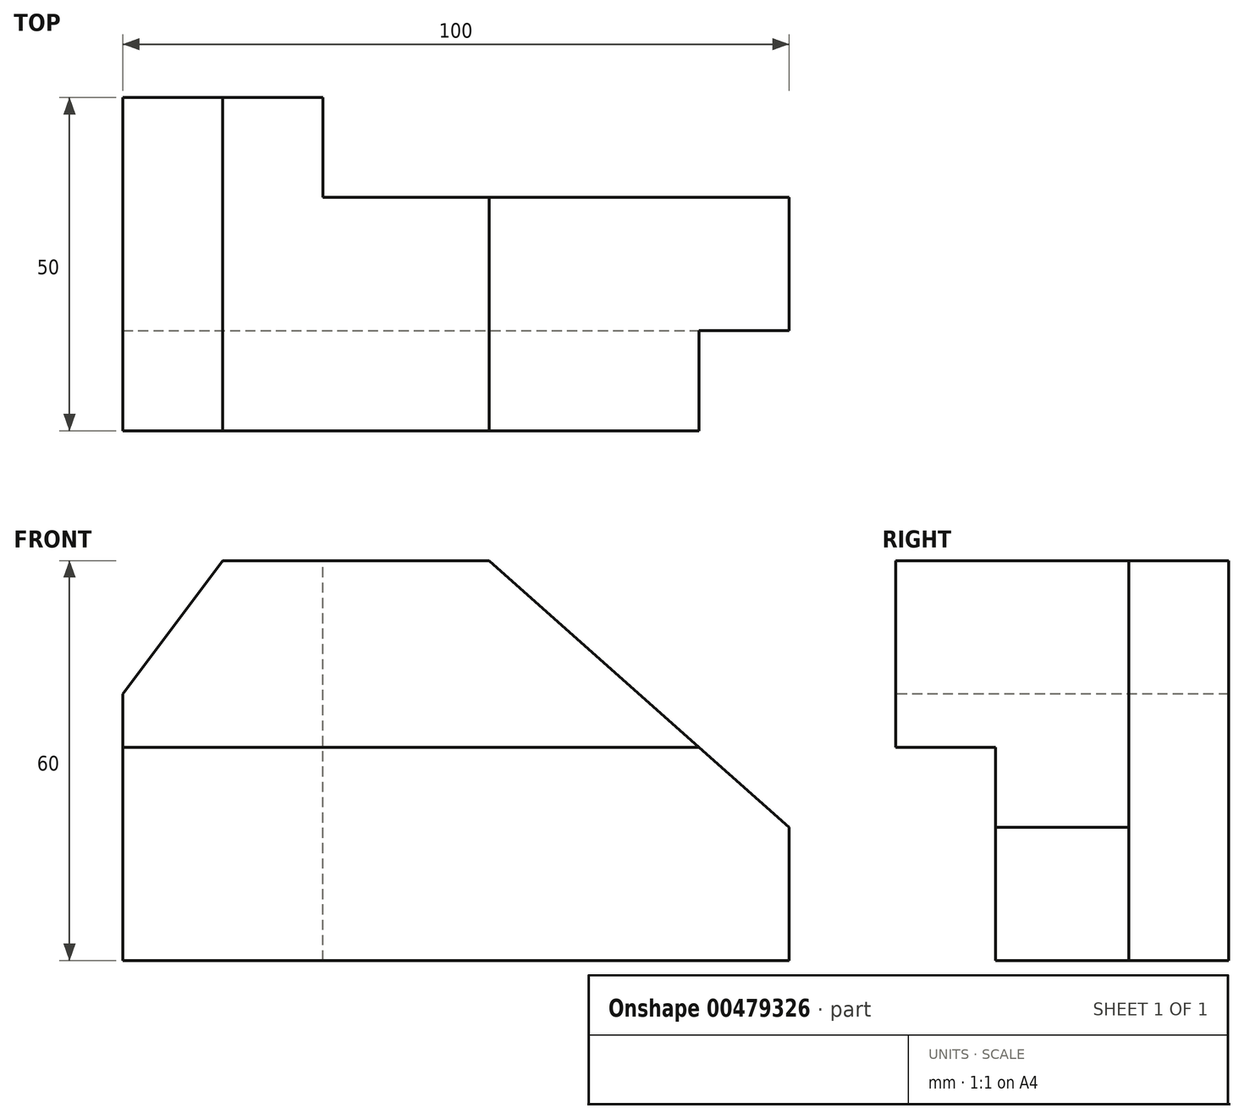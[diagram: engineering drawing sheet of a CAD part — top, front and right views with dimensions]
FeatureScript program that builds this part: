
annotation { "Feature Type Name" : "Feature", "Feature Type Description" : "" }
export const myFeature = defineFeature(function(context is Context, id is Id, definition is map)
    precondition{}
    {
        {
            var Q0;
            Q0=qCreatedBy(makeId("Front.planeOp"),FACE);
            var sketch = newSketch(context, id + "F0", { "sketchPlane" : qUnion([Q0])});
            skLineSegment(sketch, "E0.bottom", {"start": v(0, 0) * mm, "end": v(100, 0) * mm});
            skLineSegment(sketch, "E0.top", {"start": v(0, 60) * mm, "end": v(100, 60) * mm});
            skLineSegment(sketch, "E0.left", {"start": v(0, 0) * mm, "end": v(0, 60) * mm});
            skLineSegment(sketch, "E0.right", {"start": v(100, 0) * mm, "end": v(100, 60) * mm});
            skSolve(sketch);
        }
        {
            var Q0;
            Q0 = qSketchRegion(id + "F0", true);
            extrude(context, id + "F1", {"entities" : qUnion([Q0]), "oppositeDirection" : true, "depth" : 50 * mm});
        }
        {
            var Q0;
            Q0=makeQuery(id+"F1.opExtrude","SWEPT_FACE",FACE,{"disambiguationData":[OSD([sQuery(id+"F0.wireOp",EDGE,"E0.top")])]});
            var sketch = newSketch(context, id + "F2", { "sketchPlane" : qUnion([Q0])});
            skLineSegment(sketch, "E1.bottom", {"start": v(100, 50) * mm, "end": v(30, 50) * mm});
            skLineSegment(sketch, "E1.top", {"start": v(100, 35) * mm, "end": v(30, 35) * mm});
            skLineSegment(sketch, "E1.left", {"start": v(100, 50) * mm, "end": v(100, 35) * mm});
            skLineSegment(sketch, "E1.right", {"start": v(30, 50) * mm, "end": v(30, 35) * mm});
            skSolve(sketch);
        }
        {
            var Q0;
            Q0 = qSketchRegion(id + "F2", true);
            extrude(context, id + "F3", {"entities" : qUnion([Q0]), "operationType" : NewBodyOperationType.REMOVE, "endBound" : BoundingType.UP_TO_NEXT, "oppositeDirection" : true, "depth" : 25 * mm});
        }
        {
            var Q0;
            Q0=makeQuery(id+"F1.opExtrude","SWEPT_FACE",FACE,{"disambiguationData":[OSD([sQuery(id+"F0.wireOp",EDGE,"E0.right")])]});
            var sketch = newSketch(context, id + "F4", { "sketchPlane" : qUnion([Q0])});
            skLineSegment(sketch, "E2.bottom", {"start": v(0, 0) * mm, "end": v(15, 0) * mm});
            skLineSegment(sketch, "E2.top", {"start": v(0, 32) * mm, "end": v(15, 32) * mm});
            skLineSegment(sketch, "E2.left", {"start": v(0, 0) * mm, "end": v(0, 32) * mm});
            skLineSegment(sketch, "E2.right", {"start": v(15, 0) * mm, "end": v(15, 32) * mm});
            skSolve(sketch);
        }
        {
            var Q0;
            Q0 = qSketchRegion(id + "F4", true);
            extrude(context, id + "F5", {"entities" : qUnion([Q0]), "operationType" : NewBodyOperationType.REMOVE, "endBound" : BoundingType.UP_TO_NEXT, "oppositeDirection" : true, "depth" : 25 * mm});
        }
        {
            var Q0;
            Q0=makeQuery(id+"F1.opExtrude","CAP_FACE",FACE,{"disambiguationData":[OSD([sQuery(id+"F0.wireOp",EDGE,"E0.bottom"),sQuery(id+"F0.wireOp",EDGE,"E0.top"),sQuery(id+"F0.wireOp",EDGE,"E0.left"),sQuery(id+"F0.wireOp",EDGE,"E0.right")])],"isStart":true});
            var sketch = newSketch(context, id + "F6", { "sketchPlane" : qUnion([Q0])});
            skLineSegment(sketch, "E3", {"start": v(15, 60) * mm, "end": v(0, 40) * mm});
            skSolve(sketch);
        }
        {
            var Q0;
            {var subQ0=sQuery(id+"F6.wireOp",EDGE,"E3");Q0=makeQuery(id+"F6.imprint","IMPRINT",FACE,{"disambiguationData":[TD([[makeQuery(id+"F6.imprint","IMPRINT",EDGE,{"derivedFrom":subQ0}),-1.0]])]});}
            extrude(context, id + "F7", {"entities" : qUnion([Q0]), "operationType" : NewBodyOperationType.REMOVE, "endBound" : BoundingType.UP_TO_NEXT, "oppositeDirection" : true, "depth" : 25 * mm});
        }
        {
            var Q0;
            Q0=makeQuery(id+"F1.opExtrude","CAP_FACE",FACE,{"disambiguationData":[OSD([sQuery(id+"F0.wireOp",EDGE,"E0.bottom"),sQuery(id+"F0.wireOp",EDGE,"E0.top"),sQuery(id+"F0.wireOp",EDGE,"E0.left"),sQuery(id+"F0.wireOp",EDGE,"E0.right")])],"isStart":true});
            var sketch = newSketch(context, id + "F8", { "sketchPlane" : qUnion([Q0])});
            skLineSegment(sketch, "E4", {"start": v(55, 60) * mm, "end": v(100, 20) * mm});
            skPoint(sketch, "E4.endSnap0", {"position": v(100, 46) * mm});
            skSolve(sketch);
        }
        {
            var Q0;
            {var subQ3=sQuery(id+"F0.wireOp",EDGE,"E0.right");var subQ6=makeQuery(id+"F1.opExtrude","CAP_EDGE",EDGE,{"disambiguationData":[OSD([subQ3])],"isStart":true});Q0=makeQuery(id+"F8.imprint","IMPRINT",FACE,{"disambiguationData":[TD([[makeQuery(id+"F8.imprint","IMPRINT",EDGE,{"derivedFrom":subQ6}),1.0]])]});}
            extrude(context, id + "F9", {"entities" : qUnion([Q0]), "operationType" : NewBodyOperationType.REMOVE, "endBound" : BoundingType.UP_TO_NEXT, "oppositeDirection" : true, "depth" : 25 * mm});
        }
        {
            var Q0;
            Q0=makeQuery(id+"F5.boolean.opBoolean","COPY",FACE,{"derivedFrom":makeQuery(id+"F5.opExtrude","SWEPT_FACE",FACE,{"disambiguationData":[OSD([sQuery(id+"F4.wireOp",EDGE,"E2.right")])]})});
            var sketch = newSketch(context, id + "F10", { "sketchPlane" : qUnion([Q0])});
            skLineSegment(sketch, "E5", {"start": v(86.5, 32) * mm, "end": v(100, 20) * mm});
            skSolve(sketch);
        }
        {
            var Q0;
            {var subQ0=sQuery(id+"F10.wireOp",EDGE,"E5");Q0=makeQuery(id+"F10.imprint","IMPRINT",FACE,{"disambiguationData":[TD([[makeQuery(id+"F10.imprint","IMPRINT",EDGE,{"derivedFrom":subQ0}),1.0]])]});}
            extrude(context, id + "F11", {"entities" : qUnion([Q0]), "operationType" : NewBodyOperationType.REMOVE, "endBound" : BoundingType.UP_TO_NEXT, "oppositeDirection" : true, "depth" : 25 * mm});
        }
    });
